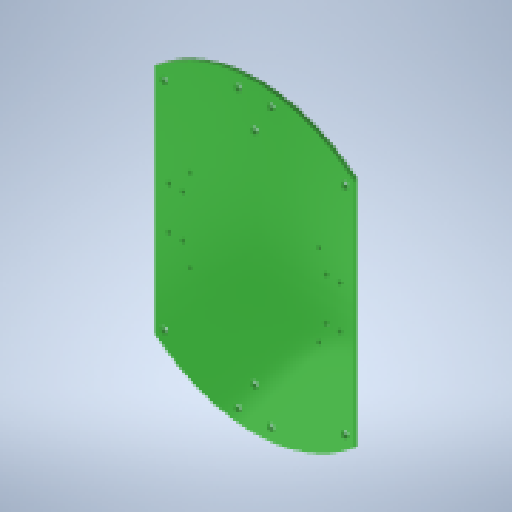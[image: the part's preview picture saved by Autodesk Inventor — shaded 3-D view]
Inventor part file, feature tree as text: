
AUTODESK INVENTOR PART (.ipt)
format: ipt  version: 2025.3 (Build 293356000, 356)  size: 195,072 bytes
history: native  units: mm
features: sketch x4, hole x3, other x1, extrude x1, mirror x1
ambient origin geometry x8: Origin, YZ Plane, XZ Plane, XY Plane, X Axis, Y Axis, Z Axis, Center Point
bodies: Body1 (feature_tree)
feature tree (10):
  other  "ソリッド1"
  extrude  "基板"  Depth=130.0mm
  hole  "モータ取付穴"  [1 undecoded]
  hole  "ボールキャスター取付穴"  [1 undecoded]
  hole  "スペーサ取付穴"  [1 undecoded]
  mirror  "ミラー1"
  sketch  "スケッチ1"
  sketch  "スケッチ2"
  sketch  "スケッチ3"
  sketch  "スケッチ4"
note: 3 required parameter values undecoded (feature->parameter linkage not recoverable at this tier; creation-order binding heuristic only, values carry confidence <= 0.55)
